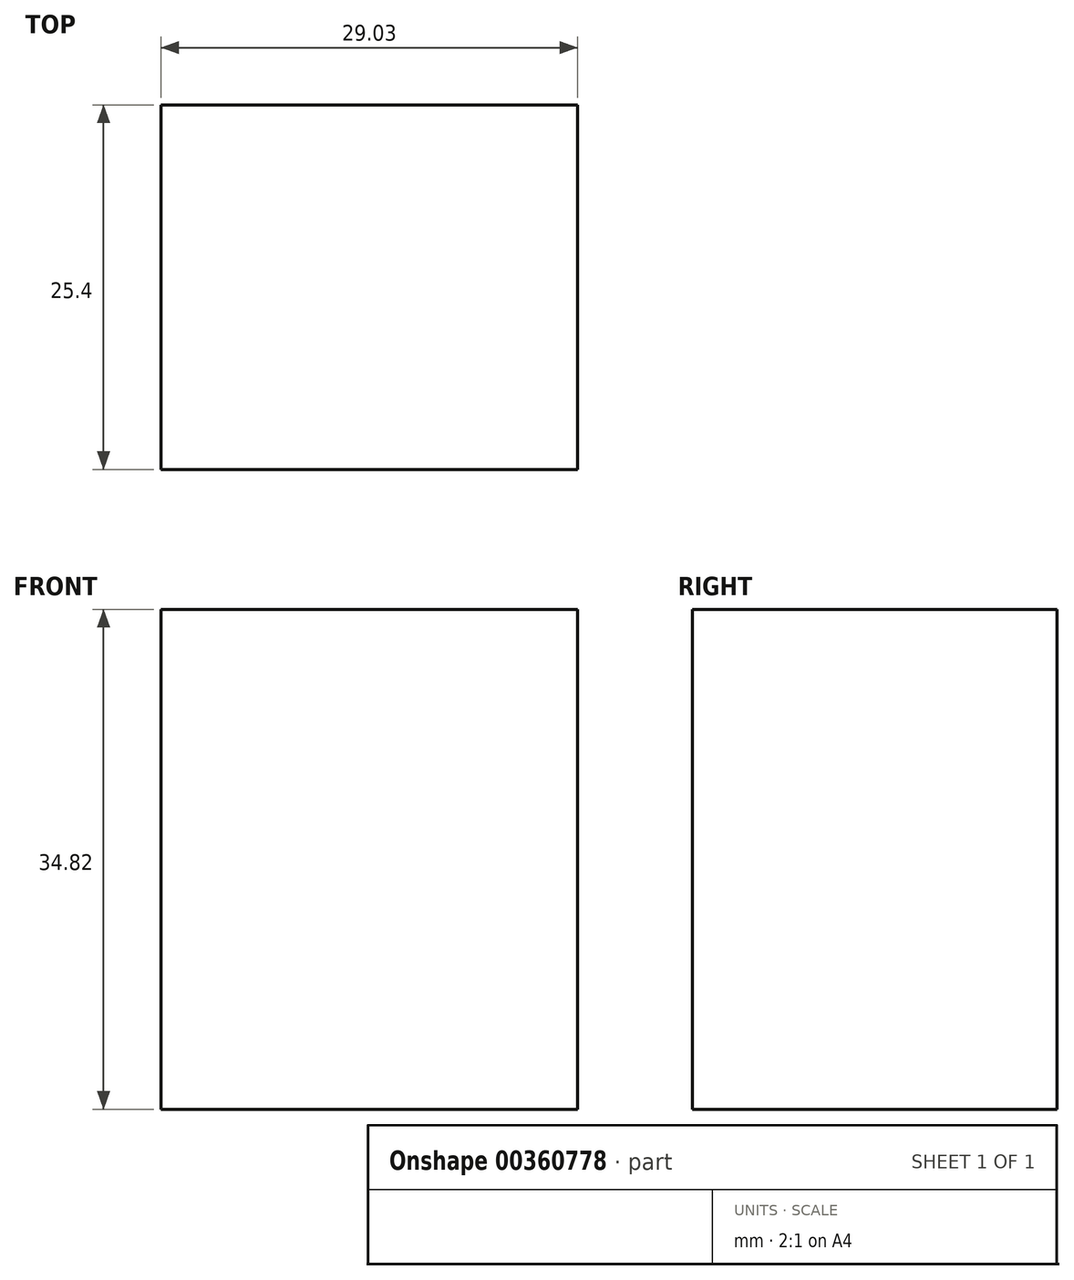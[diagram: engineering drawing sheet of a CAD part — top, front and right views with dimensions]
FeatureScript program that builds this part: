
annotation { "Feature Type Name" : "Feature", "Feature Type Description" : "" }
export const myFeature = defineFeature(function(context is Context, id is Id, definition is map)
    precondition{}
    {
        {
            var Q0;
            Q0=qCreatedBy(makeId("Front.planeOp"),FACE);
            var sketch = newSketch(context, id + "F0", { "sketchPlane" : qUnion([Q0])});
            skLineSegment(sketch, "E0.bottom", {"start": v(-53.67, 63.15) * mm, "end": v(-24.64, 63.15) * mm});
            skLineSegment(sketch, "E0.top", {"start": v(-53.67, 28.33) * mm, "end": v(-24.64, 28.33) * mm});
            skLineSegment(sketch, "E0.left", {"start": v(-53.67, 63.15) * mm, "end": v(-53.67, 28.33) * mm});
            skLineSegment(sketch, "E0.right", {"start": v(-24.64, 63.15) * mm, "end": v(-24.64, 28.33) * mm});
            skPoint(sketch, "E0.middle", {"position": v(-39.15, 45.74) * mm});
            skSolve(sketch);
        }
        {
            var Q0;
            Q0 = qSketchRegion(id + "F0", true);
            extrude(context, id + "F1", {"entities" : qUnion([Q0]), "depth" : 25.4 * mm});
        }
    });
